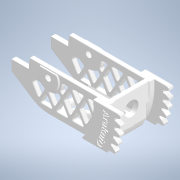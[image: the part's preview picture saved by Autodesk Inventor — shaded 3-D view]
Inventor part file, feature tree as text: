
AUTODESK INVENTOR PART (.ipt)
format: ipt  version: 2021 (Build 250183000, 183)  size: 2,562,048 bytes
history: native  units: mm
features: extrude x15, sketch x11, fillet x8, plane x4, mirror x3, projected_geometry x3, other x2, chamfer x2, hole x1
ambient origin geometry x8: Origin, YZ Plane, XZ Plane, XY Plane, X Axis, Y Axis, Z Axis, Center Point
bodies: Solid1 (feature_tree)
feature tree (49):
  other  "FDM-Slot.ipt"
  extrude  "Extrusion1"  Depth=4.6mm TaperAngle=0.0deg
  extrude  "Extrusion2"  Depth=4.1mm
  plane  "Work Plane1"
  mirror  "Mirror1"
  hole  "Hole1"  [1 undecoded]
  extrude  "Extrusion3"  Depth=2.6mm
  extrude  "Extrusion4"  Depth=2.6mm TaperAngle=0.0deg
  extrude  "Extrusion5"  Depth=74.0mm
  extrude  "Extrusion6"  Depth=2.0mm TaperAngle=0.0deg
  extrude  "Extrusion7"  Depth=215.0mm
  extrude  "Extrusion9"  Depth=8.5mm
  plane  "Work Plane3"
  extrude  "Extrusion10"  Depth=2.6mm
  plane  "Work Plane4"
  mirror  "Mirror3"
  fillet  "Fillet1"  Radius=10.0mm
  extrude  "Extrusion11"  Depth=0.5mm
  extrude  "Extrusion12"  Depth=1.0mm TaperAngle=0.0deg
  chamfer  "Chamfer1"  Distance=1.0mm
  fillet  "Fillet2"  Radius=0.5mm
  chamfer  "Chamfer2"  Distance=0.5mm
  fillet  "Fillet3"  Radius=3.2mm
  extrude  "Extrusion16"  Depth=5.5mm
  fillet  "Fillet4"  Radius=10.0mm
  extrude  "Extrusion17"  Depth=1.0mm TaperAngle=45.0deg
  fillet  "Fillet5"  Radius=2.0mm
  mirror  "Mirror4"
  fillet  "Fillet6"  Radius=1.0mm
  fillet  "Fillet7"  Radius=1.0mm
  extrude  "Extrusion18"  Depth=0.5mm
  extrude  "Extrusion19"  Depth=0.75mm TaperAngle=0.0deg
  fillet  "Fillet10"  Radius=0.35mm
  plane  "Work Plane5"
  sketch  "Sketch23"  dims[d43=10.0mm d44=0.5mm d45=1.0mm d46=0.0mm d47=1.0mm d48=0.0mm d49=0.5mm d50=2.0mm d51=45.0deg d59=0.5mm d60=3.2mm d61=5.5mm d62=10.0mm d67=1.0mm d68=2.0mm d69=45.0deg d74=2.0mm d75=1.0mm d76=1.0mm d77=3.0mm d84=12.0mm d85=120.0deg d87=120.0deg d109=0.0mm d110=0.0mm d111=0.5mm d113=0.75mm d114=0.0mm d116=0.35mm d117=0.35mm d118=0.35mm d119=0.5mm d120=0.0mm d122=0.5mm d123=0.0mm d125=180.0deg d136=0.35mm d137=0.35mm d138=6.0mm d139=0.5mm d140=2.0mm d141=8.2mm d57=0.5mm d58=0.872665mm]
  sketch  "Sketch3"  dims[d0=10.0mm d1=4.6mm d2=0.0mm]
  sketch  "Sketch5"  dims[d3=35.0mm d4=4.1mm]
  projected_geometry  "Projected Loop1"
  sketch  "Sketch6"  dims[d5=5.759587mm d6=2.6mm d7=0.0mm]
  sketch  "Sketch8"  dims[d8=3.2mm d9=6.0mm d10=6.5mm d11=3.0mm d12=90.0deg d13=8.0mm d14=20.594885mm d15=2.6mm]
  sketch  "Sketch13"  dims[d16=2.6mm d17=0.0mm d20=2.6mm d21=0.0mm]
  sketch  "Sketch14"  dims[d22=2.0mm d23=0.0mm d24=74.0mm]
  projected_geometry  "Projected Loop2"
  sketch  "Sketch15"  dims[d25=84.0mm d26=2.0mm d27=0.0mm]
  other  "SideWallCutouts"
  sketch  "Sketch20"  dims[d29=2.6mm d30=0.0mm d33=215.0mm]
  sketch  "Sketch21"  dims[d34=84.205016mm d35=8.5mm]
  sketch  "Sketch22"  dims[d36=2.6mm d37=0.0mm d39=2.6mm d41=10.0mm d42=0.0mm]
  projected_geometry  "Projected Loop3"
note: 1 required parameter value undecoded (feature->parameter linkage not recoverable at this tier; creation-order binding heuristic only, values carry confidence <= 0.55)
